# Revit family: Drain_Floor_Ligature_Resistant-Zurn-Z415LRS
name_source: partatom
category: Plumbing Fixtures
units: mm (PartAtom-declared; Revit-internal decimal feet)

## family parameters
Always vertical = Yes
Cut with Voids When Loaded = No
Maintain Annotation Orientation = No
OmniClass Number = 23.70.50.21.24.14
OmniClass Title = Deck Waste Water Drains
Part Type = Normal
Room Calculation Point = No
Round Connector Dimension = Use Diameter
Shared = No
Work Plane-Based = No

## types (52) — shared parameters
Assembly Code = D2030300
CW Connection = Yes
Description = BODY ASSEMBLY W/ TYPE LRS SQUARE LIGATURE RESISTANT STRAINER
HW Connection = Yes
Manufacturer = Zurn Water, LLC
Manufacurer Brand = Zurn
Material Main = Zurn - Cast Iron - Painted Blue
Model = Z415LRS
Product Documentation Link = https://files.zurn.com
Product Page URL = https://www.zurn.com
Product data url = https://www.bimobject.com
Strainer Open Area = 1.9 in²
URL = www.zurn.com
Vent Connection = Yes
Waste Connection = Yes
zero-valued in all types: CWFU, Default Elevation, HWFU, WFU

## per-type parameters (varying)
| type | Inside Caulk | Material Grate | Neo-Loc | No-Hub | Outlet Size (A) | Strainer Diameter (B) | Threaded | Type Comments | Weight | z_Slope Height | z_Strainer Radius | z_Strainer_Diameter |
| Z415LRS Cast Iron Body w/ 2" Inside Caulk - Outlet 5" Nickel Bronze Z400LRS | Yes | Nickel Bronze - Zurn Industries LLC - Polished | No | No | 2 in | 5 " | No | Z415-2IC-5LRS | 11.00 lb | 0.31 " | 2.5 " | 5 " |
| Z415LRS Cast Iron Body w/ 2" Inside Caulk - Outlet 6" Nickel Bronze Z400LRS | Yes | Nickel Bronze - Zurn Industries LLC - Polished | No | No | 2 in | 6 " | No | Z415-2IC-6LRS | 13.00 lb | 0.62 " | 3.03 " | 6.06 " |
| Z415LRS Cast Iron Body w/ 3" Inside Caulk - Outlet 5" Nickel Bronze Z400LRS | Yes | Nickel Bronze - Zurn Industries LLC - Polished | No | No | 3 in | 5 " | No | Z415-3IC-5LRS | 11.00 lb | 0.31 " | 2.5 " | 5 " |
| Z415LRS Cast Iron Body w/ 3" Inside Caulk - Outlet 6" Nickel Bronze Z400LRS | Yes | Nickel Bronze - Zurn Industries LLC - Polished | No | No | 3 in | 6 " | No | Z415-3IC-6LRS | 13.00 lb | 0.62 " | 3.03 " | 6.06 " |
| Z415LRS Cast Iron Body w/ 4" Inside Caulk - Outlet 5" Nickel Bronze Z400LRS | Yes | Nickel Bronze - Zurn Industries LLC - Polished | No | No | 4 in | 5 " | No | Z415-4IC-5LRS | 11.00 lb | 0.31 " | 2.5 " | 5 " |
| Z415LRS Cast Iron Body w/ 4" Inside Caulk - Outlet 6" Nickel Bronze Z400LRS | Yes | Nickel Bronze - Zurn Industries LLC - Polished | No | No | 4 in | 6 " | No | Z415-4IC-6LRS | 13.00 lb | 0.62 " | 3.03 " | 6.06 " |
| Z415LRS Cast Iron Body w/ 2" Threaded Outlet - Outlet 5" Nickel Bronze Z400LRS | No | Nickel Bronze - Zurn Industries LLC - Polished | No | No | 2 in | 5 " | Yes | Z415-2IP-5LRS | 11.00 lb | 0.31 " | 2.5 " | 5 " |
| Z415LRS Cast Iron Body w/ 2" Threaded Outlet - Outlet 6" Nickel Bronze Z400LRS | No | Nickel Bronze - Zurn Industries LLC - Polished | No | No | 2 in | 6 " | Yes | Z415-2IP-6LRS | 13.00 lb | 0.62 " | 3.03 " | 6.06 " |
| Z415LRS Cast Iron Body w/ 3" Threaded Outlet - Outlet 5" Nickel Bronze Z400LRS | No | Nickel Bronze - Zurn Industries LLC - Polished | No | No | 3 in | 5 " | Yes | Z415-3IP-5LRS | 11.00 lb | 0.31 " | 2.5 " | 5 " |
| Z415LRS Cast Iron Body w/ 3" Threaded Outlet - Outlet 6" Nickel Bronze Z400LRS | No | Nickel Bronze - Zurn Industries LLC - Polished | No | No | 3 in | 6 " | Yes | Z415-3IP-6LRS | 13.00 lb | 0.62 " | 3.03 " | 6.06 " |
| Z415LRS Cast Iron Body w/ 4" Threaded Outlet - Outlet 5" Nickel Bronze Z400LRS | No | Nickel Bronze - Zurn Industries LLC - Polished | No | No | 4 in | 5 " | Yes | Z415-4IP-5LRS | 11.00 lb | 0.31 " | 2.5 " | 5 " |
| Z415LRS Cast Iron Body w/ 4" Threaded Outlet - Outlet 6" Nickel Bronze Z400LRS | No | Nickel Bronze - Zurn Industries LLC - Polished | No | No | 4 in | 6 " | Yes | Z415-4IP-5LRS | 13.00 lb | 0.62 " | 3.03 " | 6.06 " |
| Z415LRS Cast Iron Body w/ 6" Threaded Outlet - Outlet 5" Nickel Bronze Z400LRS | No | Nickel Bronze - Zurn Industries LLC - Polished | No | No | 6 in | 5 " | Yes | Z415-6IP-6LRS | 11.00 lb | 0.31 " | 2.5 " | 5 " |
| Z415LRS Cast Iron Body w/ 6" Threaded Outlet - Outlet 6" Nickel Bronze Z400LRS | No | Nickel Bronze - Zurn Industries LLC - Polished | No | No | 6 in | 6 " | Yes | Z415-6IP-6LRS | 13.00 lb | 0.62 " | 3.03 " | 6.06 " |
| Z415LRS Cast Iron Body w/ 2" No-Hub Outlet - Outlet 5" Nickel Bronze Z400LRS | No | Nickel Bronze - Zurn Industries LLC - Polished | No | Yes | 2 in | 5 " | No | Z415-2NH-5LRS | 11.00 lb | 0.31 " | 2.5 " | 5 " |
| Z415LRS Cast Iron Body w/ 2" No-Hub Outlet - Outlet 6" Nickel Bronze Z400LRS | No | Nickel Bronze - Zurn Industries LLC - Polished | No | Yes | 2 in | 6 " | No | Z415-2NH-6LRS | 13.00 lb | 0.62 " | 3.03 " | 6.06 " |
| Z415LRS Cast Iron Body w/ 3" No-Hub Outlet - Outlet 5" Nickel Bronze Z400LRS | No | Nickel Bronze - Zurn Industries LLC - Polished | No | Yes | 3 in | 5 " | No | Z415-3NH-5LRS | 11.00 lb | 0.31 " | 2.5 " | 5 " |
| Z415LRS Cast Iron Body w/ 3" No-Hub Outlet - Outlet 6" Nickel Bronze Z400LRS | No | Nickel Bronze - Zurn Industries LLC - Polished | No | Yes | 3 in | 6 " | No | Z415-3NH-6LRS | 13.00 lb | 0.62 " | 3.03 " | 6.06 " |
| Z415LRS Cast Iron Body w/ 4" No-Hub Outlet - Outlet 5" Nickel Bronze Z400LRS | No | Nickel Bronze - Zurn Industries LLC - Polished | No | Yes | 4 in | 5 " | No | Z415-4NH-5LRS | 11.00 lb | 0.31 " | 2.5 " | 5 " |
| Z415LRS Cast Iron Body w/ 4" No-Hub Outlet - Outlet 6" Nickel Bronze Z400LRS | No | Nickel Bronze - Zurn Industries LLC - Polished | No | Yes | 4 in | 6 " | No | Z415-4NH-6LRS | 13.00 lb | 0.62 " | 3.03 " | 6.06 " |
| Z415LRS Cast Iron Body w/ 2" Neo-Loc Outlet - Outlet 5" Nickel Bronze Z400LRS | No | Nickel Bronze - Zurn Industries LLC - Polished | Yes | No | 2 in | 5 " | No | Z415-2NL-5LRS | 11.00 lb | 0.31 " | 2.5 " | 5 " |
| Z415LRS Cast Iron Body w/ 2" Neo-Loc Outlet - Outlet 6" Nickel Bronze Z400LRS | No | Nickel Bronze - Zurn Industries LLC - Polished | Yes | No | 2 in | 6 " | No | Z415-2NL-6LRS | 13.00 lb | 0.62 " | 3.03 " | 6.06 " |
| Z415LRS Cast Iron Body w/ 3" Neo-Loc Outlet - Outlet 5" Nickel Bronze Z400LRS | No | Nickel Bronze - Zurn Industries LLC - Polished | Yes | No | 3 in | 5 " | No | Z415-3NL-5LRS | 11.00 lb | 0.31 " | 2.5 " | 5 " |
| Z415LRS Cast Iron Body w/ 3" Neo-Loc Outlet - Outlet 6" Nickel Bronze Z400LRS | No | Nickel Bronze - Zurn Industries LLC - Polished | Yes | No | 3 in | 6 " | No | Z415-3NL-6LRS | 13.00 lb | 0.62 " | 3.03 " | 6.06 " |
| Z415LRS Cast Iron Body w/ 4" Neo-Loc Outlet - Outlet 5" Nickel Bronze Z400LRS | No | Nickel Bronze - Zurn Industries LLC - Polished | Yes | No | 4 in | 5 " | No | Z415-4NL-5LRS | 11.00 lb | 0.31 " | 2.5 " | 5 " |
| Z415LRS Cast Iron Body w/ 4" Neo-Loc Outlet - Outlet 6" Nickel Bronze Z400LRS | No | Nickel Bronze - Zurn Industries LLC - Polished | Yes | No | 4 in | 6 " | No | Z415-4NL-6LRS | 13.00 lb | 0.62 " | 3.03 " | 6.06 " |
| Z415LRS Cast Iron Body w/ 2" Inside Caulk - Outlet 5" Stainless Steel Z400LRS | Yes | Steel - Zurn Industries - Stainless | No | No | 2 in | 5 " | No | Z415-2IC-5LRS | 11.00 lb | 0.31 " | 2.5 " | 5 " |
| Z415LRS Cast Iron Body w/ 2" Inside Caulk - Outlet 6" Stainless Steel Z400LRS | Yes | Steel - Zurn Industries - Stainless | No | No | 2 in | 6 " | No | Z415-2IC-6LRS | 13.00 lb | 0.62 " | 3.03 " | 6.06 " |
| Z415LRS Cast Iron Body w/ 3" Inside Caulk - Outlet 5" Stainless Steel Z400LRS | Yes | Steel - Zurn Industries - Stainless | No | No | 3 in | 5 " | No | Z415-3IC-5LRS | 11.00 lb | 0.31 " | 2.5 " | 5 " |
| Z415LRS Cast Iron Body w/ 3" Inside Caulk - Outlet 6" Stainless Steel Z400LRS | Yes | Steel - Zurn Industries - Stainless | No | No | 3 in | 6 " | No | Z415-3IC-6LRS | 13.00 lb | 0.62 " | 3.03 " | 6.06 " |
| Z415LRS Cast Iron Body w/ 4" Inside Caulk - Outlet 5" Stainless Steel Z400LRS | Yes | Steel - Zurn Industries - Stainless | No | No | 4 in | 5 " | No | Z415-4IC-5LRS | 11.00 lb | 0.31 " | 2.5 " | 5 " |
| Z415LRS Cast Iron Body w/ 4" Inside Caulk - Outlet 6" Stainless Steel Z400LRS | Yes | Steel - Zurn Industries - Stainless | No | No | 4 in | 6 " | No | Z415-4IC-6LRS | 13.00 lb | 0.62 " | 3.03 " | 6.06 " |
| Z415LRS Cast Iron Body w/ 2" Threaded Outlet - Outlet 5" Stainless Steel Z400LRS | No | Steel - Zurn Industries - Stainless | No | No | 2 in | 5 " | Yes | Z415-2IP-5LRS | 11.00 lb | 0.31 " | 2.5 " | 5 " |
| Z415LRS Cast Iron Body w/ 2" Threaded Outlet - Outlet 6" Stainless Steel Z400LRS | No | Steel - Zurn Industries - Stainless | No | No | 2 in | 6 " | Yes | Z415-2IP-6LRS | 13.00 lb | 0.62 " | 3.03 " | 6.06 " |
| Z415LRS Cast Iron Body w/ 3" Threaded Outlet - Outlet 5" Stainless Steel Z400LRS | No | Steel - Zurn Industries - Stainless | No | No | 3 in | 5 " | Yes | Z415-3IP-5LRS | 11.00 lb | 0.31 " | 2.5 " | 5 " |
| Z415LRS Cast Iron Body w/ 3" Threaded Outlet - Outlet 6" Stainless Steel Z400LRS | No | Steel - Zurn Industries - Stainless | No | No | 3 in | 6 " | Yes | Z415-3IP-6LRS | 13.00 lb | 0.62 " | 3.03 " | 6.06 " |
| Z415LRS Cast Iron Body w/ 4" Threaded Outlet - Outlet 5" Stainless Steel Z400LRS | No | Steel - Zurn Industries - Stainless | No | No | 4 in | 5 " | Yes | Z415-4IP-5LRS | 11.00 lb | 0.31 " | 2.5 " | 5 " |
| Z415LRS Cast Iron Body w/ 4" Threaded Outlet - Outlet 6" Stainless Steel Z400LRS | No | Steel - Zurn Industries - Stainless | No | No | 4 in | 6 " | Yes | Z415-4IP-6LRS | 13.00 lb | 0.62 " | 3.03 " | 6.06 " |
| Z415LRS Cast Iron Body w/ 6" Threaded Outlet - Outlet 5" Stainless Steel Z400LRS | No | Steel - Zurn Industries - Stainless | No | No | 6 in | 5 " | Yes | Z415-6IP-5LRS | 11.00 lb | 0.31 " | 2.5 " | 5 " |
| Z415LRS Cast Iron Body w/ 6" Threaded Outlet - Outlet 6" Stainless Steel Z400LRS | No | Steel - Zurn Industries - Stainless | No | No | 6 in | 6 " | Yes | Z415-6IP-6LRS | 13.00 lb | 0.62 " | 3.03 " | 6.06 " |
| Z415LRS Cast Iron Body w/ 2" No-Hub Outlet - Outlet 5" Stainless Steel Z400LRS | No | Steel - Zurn Industries - Stainless | No | Yes | 2 in | 5 " | No | Z415-2NH-5LRS | 11.00 lb | 0.31 " | 2.5 " | 5 " |
| Z415LRS Cast Iron Body w/ 2" No-Hub Outlet - Outlet 6" Stainless Steel Z400LRS | No | Steel - Zurn Industries - Stainless | No | Yes | 2 in | 6 " | No | Z415-2NH-6LRS | 13.00 lb | 0.62 " | 3.03 " | 6.06 " |
| Z415LRS Cast Iron Body w/ 3" No-Hub Outlet - Outlet 5" Stainless Steel Z400LRS | No | Steel - Zurn Industries - Stainless | No | Yes | 3 in | 5 " | No | Z415-3NH-5LRS | 11.00 lb | 0.31 " | 2.5 " | 5 " |
| Z415LRS Cast Iron Body w/ 3" No-Hub Outlet - Outlet 6" Stainless Steel Z400LRS | No | Steel - Zurn Industries - Stainless | No | Yes | 3 in | 6 " | No | Z415-3NH-6LRS | 13.00 lb | 0.62 " | 3.03 " | 6.06 " |
| Z415LRS Cast Iron Body w/ 4" No-Hub Outlet - Outlet 5" Stainless Steel Z400LRS | No | Steel - Zurn Industries - Stainless | No | Yes | 4 in | 5 " | No | Z415-4NH-5LRS | 11.00 lb | 0.31 " | 2.5 " | 5 " |
| Z415LRS Cast Iron Body w/ 4" No-Hub Outlet - Outlet 6" Stainless Steel Z400LRS | No | Steel - Zurn Industries - Stainless | No | Yes | 4 in | 6 " | No | Z415-4NH-6LRS | 13.00 lb | 0.62 " | 3.03 " | 6.06 " |
| Z415LRS Cast Iron Body w/ 2" Neo-Loc Outlet - Outlet 5" Stainless Steel Z400LRS | No | Steel - Zurn Industries - Stainless | Yes | No | 2 in | 5 " | No | Z415-2NL-5LRS | 11.00 lb | 0.31 " | 2.5 " | 5 " |
| Z415LRS Cast Iron Body w/ 2" Neo-Loc Outlet - Outlet 6" Stainless Steel Z400LRS | No | Steel - Zurn Industries - Stainless | Yes | No | 2 in | 6 " | No | Z415-2NL-6LRS | 13.00 lb | 0.62 " | 3.03 " | 6.06 " |
| Z415LRS Cast Iron Body w/ 3" Neo-Loc Outlet - Outlet 5" Stainless Steel Z400LRS | No | Steel - Zurn Industries - Stainless | Yes | No | 3 in | 5 " | No | Z415-3NL-5LRS | 11.00 lb | 0.31 " | 2.5 " | 5 " |
| Z415LRS Cast Iron Body w/ 3" Neo-Loc Outlet - Outlet 6" Stainless Steel Z400LRS | No | Steel - Zurn Industries - Stainless | Yes | No | 3 in | 6 " | No | Z415-3NL-6LRS | 13.00 lb | 0.62 " | 3.03 " | 6.06 " |
| Z415LRS Cast Iron Body w/ 4" Neo-Loc Outlet - Outlet 5" Stainless Steel Z400LRS | No | Steel - Zurn Industries - Stainless | Yes | No | 4 in | 5 " | No | Z415-4NL-5LRS | 11.00 lb | 0.31 " | 2.5 " | 5 " |
| Z415LRS Cast Iron Body w/ 4" Neo-Loc Outlet - Outlet 6" Stainless Steel Z400LRS | No | Steel - Zurn Industries - Stainless | Yes | No | 4 in | 6 " | No | Z415-4NL-6LRS | 13.00 lb | 0.62 " | 3.03 " | 6.06 " |

## geometry (parser evidence)
native form markers: Sweep x2
no freeform markers — native parametric forms only
